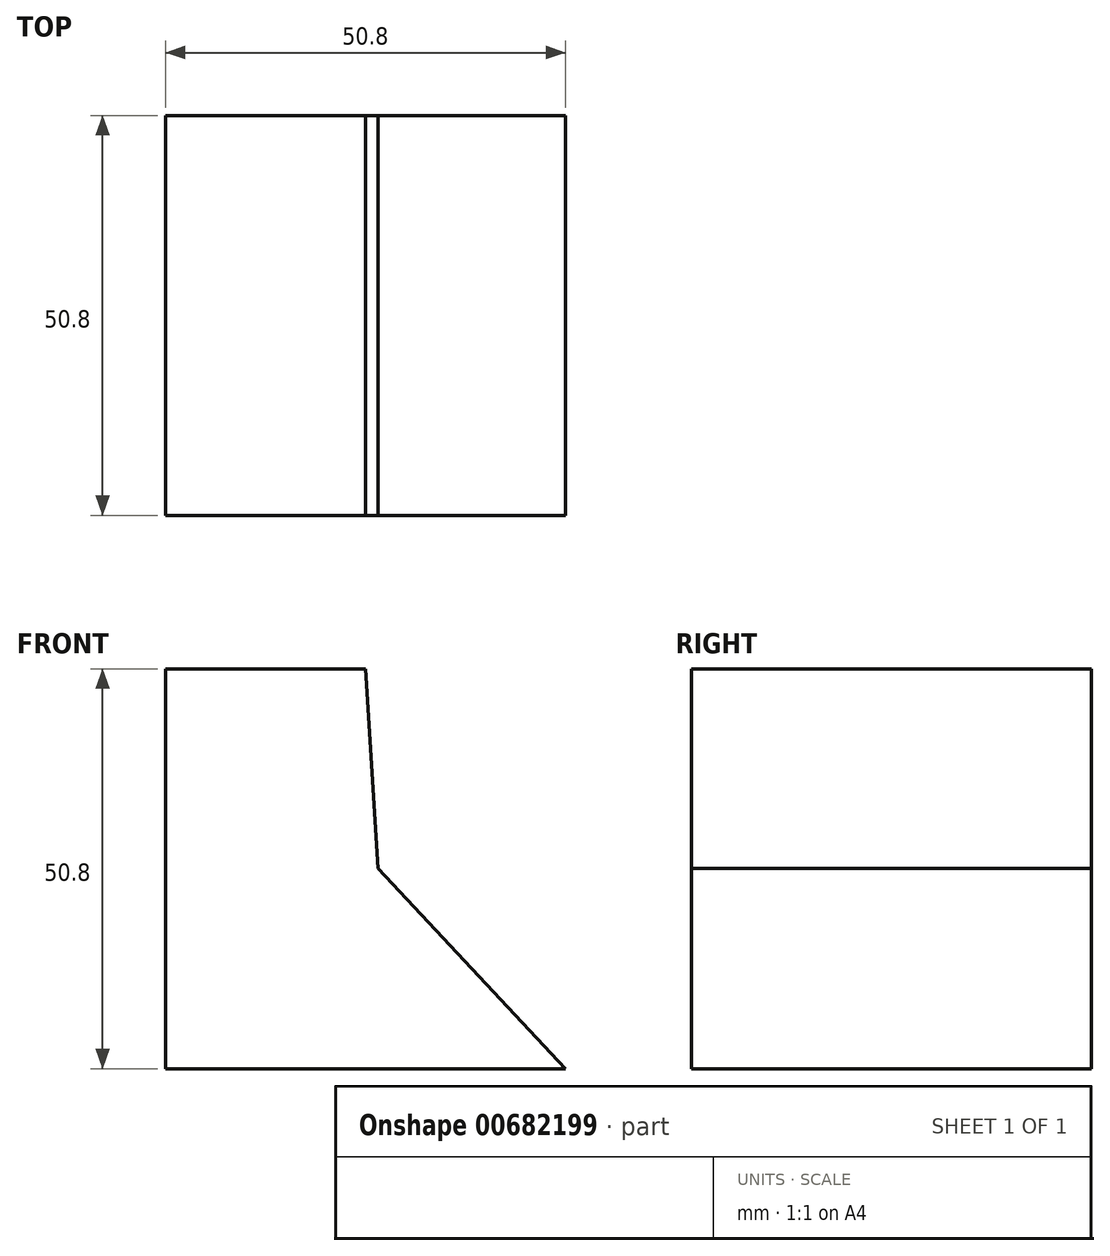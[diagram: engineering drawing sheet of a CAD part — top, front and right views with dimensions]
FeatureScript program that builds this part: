
annotation { "Feature Type Name" : "Feature", "Feature Type Description" : "" }
export const myFeature = defineFeature(function(context is Context, id is Id, definition is map)
    precondition{}
    {
        {
            var Q0;
            Q0=qCreatedBy(makeId("Front.planeOp"),FACE);
            var sketch = newSketch(context, id + "F0", { "sketchPlane" : qUnion([Q0])});
            skLineSegment(sketch, "E0", {"start": v(-33.9, 40.01) * mm, "end": v(-33.9, -10.79) * mm});
            skLineSegment(sketch, "E1", {"start": v(-33.9, -10.79) * mm, "end": v(16.9, -10.79) * mm});
            skLineSegment(sketch, "E2", {"start": v(-33.9, 40.01) * mm, "end": v(-8.5, 40.01) * mm});
            skLineSegment(sketch, "E3", {"start": v(-8.5, 40.01) * mm, "end": v(-6.89, 14.66) * mm});
            skLineSegment(sketch, "E4", {"start": v(-6.89, 14.66) * mm, "end": v(16.9, -10.79) * mm});
            skSolve(sketch);
        }
        {
            var Q0;
            Q0 = qSketchRegion(id + "F0", true);
            extrude(context, id + "F1", {"entities" : qUnion([Q0]), "depth" : 50.8 * mm, "offsetDistance" : 25.4 * mm});
        }
    });
